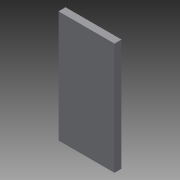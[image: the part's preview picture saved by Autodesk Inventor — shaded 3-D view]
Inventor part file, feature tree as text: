
AUTODESK INVENTOR PART (.ipt)
format: ipt  version: 2016 (Build 200138000, 138)  size: 69,632 bytes
history: native  units: in
note: dims shown in document units (in); Inventor stores cm internally (conversion verified against a paired STEP export)
features: extrude x1, sketch x1
ambient origin geometry x8: Origin, YZ Plane, XZ Plane, XY Plane, X Axis, Y Axis, Z Axis, Center Point
bodies: Solid1 (feature_tree)
feature tree (2):
  extrude  "Extrusion1"  Depth=2.0in
  sketch  "Sketch1"  dims[d0=1.0in d1=2.0in d2=0.125in d3=0.0in]
